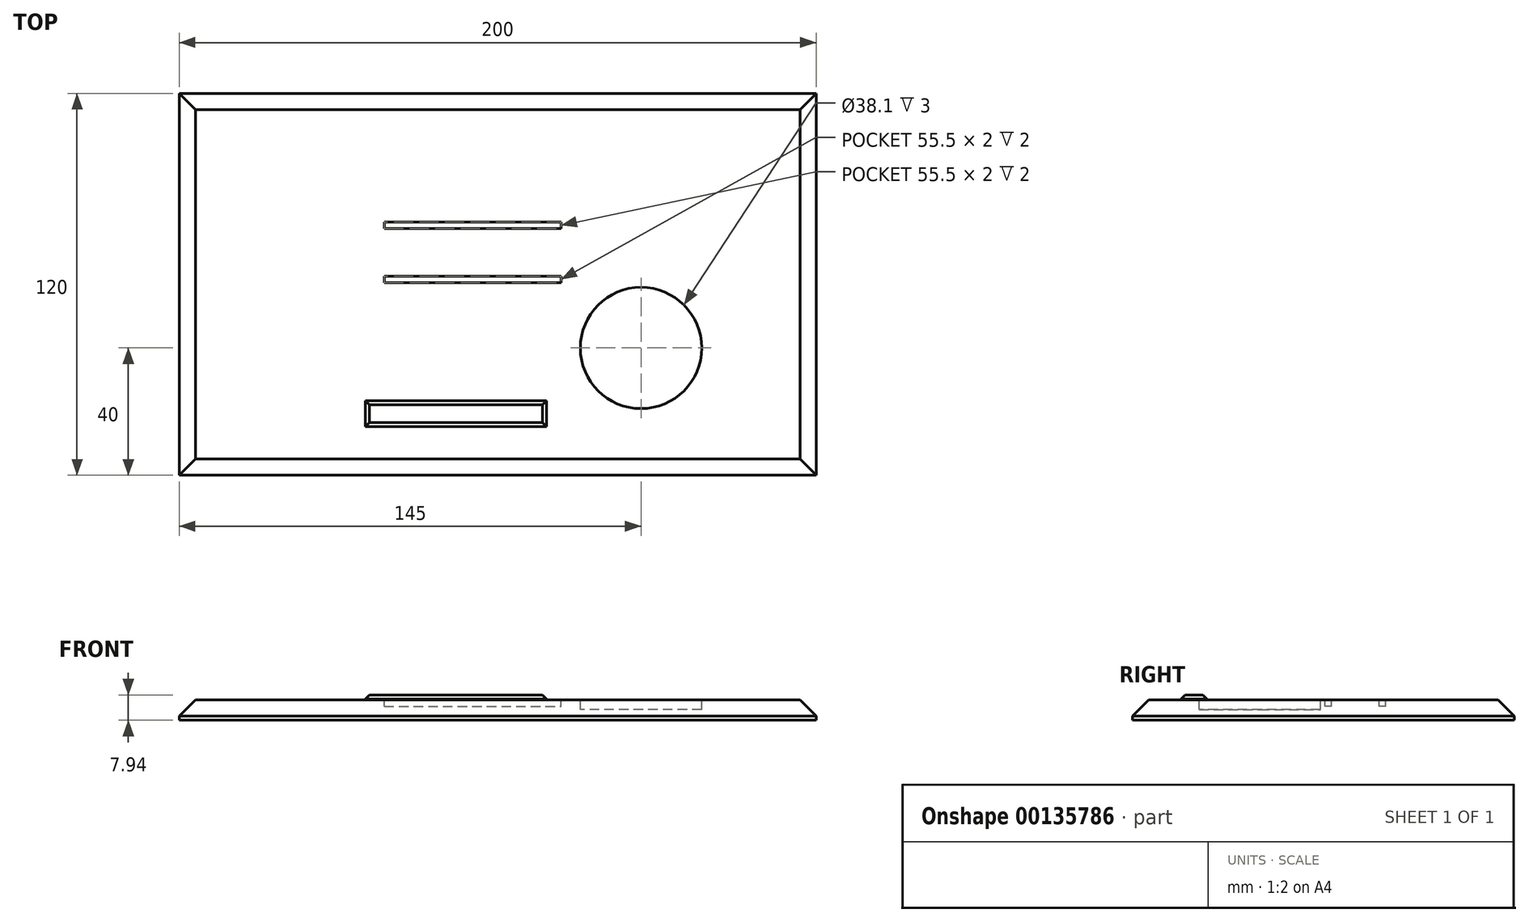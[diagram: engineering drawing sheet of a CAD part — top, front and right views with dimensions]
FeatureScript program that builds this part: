
annotation { "Feature Type Name" : "Feature", "Feature Type Description" : "" }
export const myFeature = defineFeature(function(context is Context, id is Id, definition is map)
    precondition{}
    {
        {
            var Q0;
            Q0=qCreatedBy(makeId("Top.planeOp"),FACE);
            var sketch = newSketch(context, id + "F0", { "sketchPlane" : qUnion([Q0])});
            skLineSegment(sketch, "E0.bottom", {"start": v(0, 0) * mm, "end": v(-200, 0) * mm});
            skLineSegment(sketch, "E0.top", {"start": v(0, 120) * mm, "end": v(-200, 120) * mm});
            skLineSegment(sketch, "E0.left", {"start": v(0, 0) * mm, "end": v(0, 120) * mm});
            skLineSegment(sketch, "E0.right", {"start": v(-200, 0) * mm, "end": v(-200, 120) * mm});
            skSolve(sketch);
        }
        {
            var Q0;
            Q0 = qSketchRegion(id + "F0", true);
            var Q1;
            Q1=makeQuery(id+"F0.imprint","IMPRINT",FACE,{"disambiguationData":[TD([[makeQuery(id+"F0.imprint","IMPRINT",EDGE,{"derivedFrom":sQuery(id+"F0.wireOp",EDGE,"E0.bottom")}),-1.0]])]});
            extrude(context, id + "F1", {"entities" : qUnion([Q0, Q1]), "depth" : 6.35 * mm});
        }
        {
            var Q0;
            Q0=makeQuery(id+"F1.opExtrude","CAP_FACE",FACE,{"disambiguationData":[OSD([sQuery(id+"F0.wireOp",EDGE,"E0.bottom"),sQuery(id+"F0.wireOp",EDGE,"E0.top"),sQuery(id+"F0.wireOp",EDGE,"E0.left"),sQuery(id+"F0.wireOp",EDGE,"E0.right")])],"isStart":false});
            var sketch = newSketch(context, id + "F2", { "sketchPlane" : qUnion([Q0])});
            skCircle(sketch, "E1", {"center": v(-55, 40) * mm, "radius": 19.05 * mm});
            skLineSegment(sketch, "E2", {"start": v(-55, 40) * mm, "end": v(-55, 0) * mm, "construction": true});
            skLineSegment(sketch, "E3", {"start": v(-55, 0) * mm, "end": v(0, 0) * mm, "construction": true});
            skLineSegment(sketch, "E4.0", {"start": v(0, 120) * mm, "end": v(-200, 120) * mm});
            skLineSegment(sketch, "E5.0", {"start": v(0, 0) * mm, "end": v(-200, 0) * mm});
            skSolve(sketch);
        }
        {
            var Q0;
            Q0=makeQuery(id+"F1.opExtrude","CAP_EDGE",EDGE,{"disambiguationData":[OSD([sQuery(id+"F0.wireOp",EDGE,"E0.right")])],"isStart":false});
            var Q1;
            Q1=makeQuery(id+"F1.opExtrude","CAP_EDGE",EDGE,{"disambiguationData":[OSD([sQuery(id+"F0.wireOp",EDGE,"E0.top")])],"isStart":false});
            var Q2;
            Q2=makeQuery(id+"F1.opExtrude","CAP_FACE",FACE,{"disambiguationData":[OSD([sQuery(id+"F0.wireOp",EDGE,"E0.bottom"),sQuery(id+"F0.wireOp",EDGE,"E0.top"),sQuery(id+"F0.wireOp",EDGE,"E0.left"),sQuery(id+"F0.wireOp",EDGE,"E0.right")])],"isStart":false});
            chamfer(context, id + "F3", {"entities" : qUnion([Q0, Q1, Q2]), "width" : 5.08 * mm, "tangentPropagation" : true});
        }
        {
            var Q0;
            Q0=makeQuery(id+"F1.opExtrude","CAP_FACE",FACE,{"disambiguationData":[OSD([sQuery(id+"F0.wireOp",EDGE,"E0.bottom"),sQuery(id+"F0.wireOp",EDGE,"E0.top"),sQuery(id+"F0.wireOp",EDGE,"E0.left"),sQuery(id+"F0.wireOp",EDGE,"E0.right")])],"isStart":false});
            var sketch = newSketch(context, id + "F4", { "sketchPlane" : qUnion([Q0])});
            skLineSegment(sketch, "E6.bottom", {"start": v(-141.57, 23.45) * mm, "end": v(-84.65, 23.45) * mm});
            skLineSegment(sketch, "E6.top", {"start": v(-141.57, 15.3) * mm, "end": v(-84.65, 15.3) * mm});
            skLineSegment(sketch, "E6.left", {"start": v(-141.57, 23.45) * mm, "end": v(-141.57, 15.3) * mm});
            skLineSegment(sketch, "E6.right", {"start": v(-84.65, 23.45) * mm, "end": v(-84.65, 15.3) * mm});
            skLineSegment(sketch, "E7", {"start": v(-113.11, 5.08) * mm, "end": v(-113.11, 38.53) * mm, "construction": true});
            skPoint(sketch, "E7.startSnap0", {"position": v(-113.11, 23.45) * mm});
            skPoint(sketch, "E7.startSnap1", {"position": v(-100, 5.08) * mm});
            skSolve(sketch);
        }
        {
            var Q0;
            Q0 = qSketchRegion(id + "F4", true);
            extrude(context, id + "F5", {"entities" : qUnion([Q0]), "operationType" : NewBodyOperationType.ADD, "depth" : 1.59 * mm});
        }
        {
            var Q0;
            Q0=makeQuery(id+"F5.opExtrude","CAP_EDGE",EDGE,{"disambiguationData":[OSD([sQuery(id+"F4.wireOp",EDGE,"E6.top")])],"isStart":false});
            var Q1;
            Q1=makeQuery(id+"F5.opExtrude","CAP_EDGE",EDGE,{"disambiguationData":[OSD([sQuery(id+"F4.wireOp",EDGE,"E6.left")])],"isStart":false});
            var Q2;
            Q2=makeQuery(id+"F5.opExtrude","CAP_EDGE",EDGE,{"disambiguationData":[OSD([sQuery(id+"F4.wireOp",EDGE,"E6.bottom")])],"isStart":false});
            var Q3;
            Q3=makeQuery(id+"F5.opExtrude","CAP_EDGE",EDGE,{"disambiguationData":[OSD([sQuery(id+"F4.wireOp",EDGE,"E6.right")])],"isStart":false});
            chamfer(context, id + "F6", {"entities" : qUnion([Q0, Q1, Q2, Q3]), "width" : 1.27 * mm, "tangentPropagation" : true});
        }
        {
            var Q0;
            Q0=makeQuery(id+"F2.imprint","IMPRINT",FACE,{"disambiguationData":[TD([[makeQuery(id+"F2.imprint","IMPRINT",EDGE,{"derivedFrom":sQuery(id+"F2.wireOp",EDGE,"E1")}),1.0]])]});
            extrude(context, id + "F7", {"entities" : qUnion([Q0]), "operationType" : NewBodyOperationType.REMOVE, "oppositeDirection" : true, "depth" : 3 * mm});
        }
        {
            var Q0;
            Q0=makeQuery(id+"F2.imprint","IMPRINT",FACE,{"disambiguationData":[TD([[makeQuery(id+"F2.imprint","IMPRINT",EDGE,{"derivedFrom":sQuery(id+"F2.wireOp",EDGE,"E1")}),-1.0]])]});
            var sketch = newSketch(context, id + "F8", { "sketchPlane" : qUnion([Q0])});
            skLineSegment(sketch, "E8.bottom", {"start": v(-135.63, 79.55) * mm, "end": v(-80.13, 79.55) * mm});
            skLineSegment(sketch, "E8.top", {"start": v(-135.63, 77.55) * mm, "end": v(-80.13, 77.55) * mm});
            skLineSegment(sketch, "E8.left", {"start": v(-135.63, 79.55) * mm, "end": v(-135.63, 77.55) * mm});
            skLineSegment(sketch, "E8.right", {"start": v(-80.13, 79.55) * mm, "end": v(-80.13, 77.55) * mm});
            skLineSegment(sketch, "E9.bottom", {"start": v(-135.63, 62.55) * mm, "end": v(-80.13, 62.55) * mm});
            skLineSegment(sketch, "E9.top", {"start": v(-135.63, 60.55) * mm, "end": v(-80.13, 60.55) * mm});
            skLineSegment(sketch, "E9.left", {"start": v(-135.63, 62.55) * mm, "end": v(-135.63, 60.55) * mm});
            skLineSegment(sketch, "E9.right", {"start": v(-80.13, 62.55) * mm, "end": v(-80.13, 60.55) * mm});
            skSolve(sketch);
        }
        {
            var Q0;
            Q0 = qSketchRegion(id + "F8", true);
            extrude(context, id + "F9", {"entities" : qUnion([Q0]), "operationType" : NewBodyOperationType.REMOVE, "oppositeDirection" : true, "depth" : 2 * mm});
        }
    });
